# Revit family: KS Husky, Typ IV-19, M 8-M10, Ø 10- 76,1
name_source: partatom
category: HLS-Bauteile
revit_build: Autodesk Revit 2017 (Build: 20190507_1515(x64)
units: mm (PartAtom-declared; Revit-internal decimal feet)

## family parameters
Arbeitsebenenbasiert = Ja
Beim Laden mit Abzugskörper schneiden = Nein
Bemaßung runder Anschluss = Durchmesser verwenden
Gemeinsam genutzt = Ja
Immer vertikal = Nein
Raumberechnungspunkt = Nein
Teiletyp = Normal

## types (20) — shared parameters
Anschluss = M8/M10
Baustoffklasse = B2
DVS = 5 mm  [stored 0.0164042 ft]
Dichte Kern = 120 kg/m³
Dämmkörper = KA/PU
Fabrikat = MEFA
Firma = MEFA Befestigungs- und Montagesysteme GmbH
H1 = 2 mm  [stored 0.00656168 ft]
HGA = 16 mm  [stored 0.0524934 ft]
Kurztext1 = Kälteschelle Husky IV 19
Material = Stahl
Material Mantel = Kunststoff
Materialname = DD11
Mengeneinheit = St
Oberflaeche = galvanisch verzinkt
Rohrschellentyp = Trabant
Typ = IV 19
Vorgabe-Ansicht = 1219 mm
Wasserdampfdiffusionswiderstand = 7000 µ
Wärmeleitfähigkeit = 0.029 W/mK
max. Temperaturbeständigkeit = 105 °C
mittl. Nenndruckfestigkeit Kern = 1,35 N/mm²
stat. Belastung Kern = 0,27 N/mm²

## per-type parameters (varying)
- Kälteschelle Husky, Typ IV-19, M8/M10, Ø 10: A=38 mm  [stored 0.124672 ft]; Anschlußhöhe=39 mm; Artikelnummer=6840100; B=92 mm; Breite=88 mm; D=10 mm  [stored 0.0328084 ft]; D0=51 mm  [stored 0.167323 ft]; DF1=19 mm  [stored 0.062336 ft]; DF2=19 mm  [stored 0.062336 ft]; DS=21 mm  [stored 0.0688976 ft]; Dämmstärke=21 mm  [stored 0.0688976 ft]; EAN=4250928454652; Gewicht=0.09 kg; Gewicht pro Bauteil=0.09 kg; H=70 mm; H2=3 mm  [stored 0.00984252 ft]; Kurztext2=10 mm Iso 21 x 36 mm M8/M10; L=36 mm  [stored 0.11811 ft]; MB=20 mm  [stored 0.0656168 ft]; MD=2 mm  [stored 0.00656168 ft]; R=26 mm; RM=27 mm  [stored 0.0885827 ft]; Rohraußendurchmesser Kunststoff=10 mm; Rohraußendurchmesser Kupfer=10 mm; S=73 mm; Schalenlänge=36 mm; max. zul. Last=0.10 kN; vpe=24 St
- Kälteschelle Husky, Typ IV-19, M8/M10, Ø 12: A=37 mm  [stored 0.121391 ft]; Anschlußhöhe=38 mm; Artikelnummer=6840120; B=92 mm; Breite=88 mm; D=12 mm  [stored 0.0393701 ft]; D0=51 mm  [stored 0.167323 ft]; DF1=19 mm  [stored 0.062336 ft]; DF2=19 mm  [stored 0.062336 ft]; DS=20 mm  [stored 0.0656168 ft]; Dämmstärke=20 mm  [stored 0.0656168 ft]; EAN=4250928440662; Gewicht=0.09 kg; Gewicht pro Bauteil=0.09 kg; H=70 mm; H2=3 mm  [stored 0.00984252 ft]; Kurztext2=12 mm Iso 20 x 36 mm M8/M10; L=36 mm  [stored 0.11811 ft]; MB=20 mm  [stored 0.0656168 ft]; MD=2 mm  [stored 0.00656168 ft]; R=26 mm; RM=27 mm  [stored 0.0885827 ft]; Rohraußendurchmesser Kunststoff=12 mm; Rohraußendurchmesser Kupfer=12 mm; S=73 mm; Schalenlänge=36 mm; max. zul. Last=0.10 kN; vpe=24 St
- Kälteschelle Husky, Typ IV-19, M8/M10, Ø 15: A=36 mm  [stored 0.11811 ft]; Anschlußhöhe=37 mm; Artikelnummer=6840150; B=92 mm; Breite=88 mm; D=15 mm  [stored 0.0492126 ft]; D0=51 mm  [stored 0.167323 ft]; DF1=19 mm  [stored 0.062336 ft]; DF2=19 mm  [stored 0.062336 ft]; DS=18 mm  [stored 0.0590551 ft]; Dämmstärke=18 mm  [stored 0.0590551 ft]; EAN=4250928440679; Gewicht=0.09 kg; Gewicht pro Bauteil=0.09 kg; H=70 mm; H2=3 mm  [stored 0.00984252 ft]; Kurztext2=15 mm Iso 18 x 36 mm M8/M10; L=36 mm  [stored 0.11811 ft]; MB=20 mm  [stored 0.0656168 ft]; MD=2 mm  [stored 0.00656168 ft]; R=26 mm; RM=27 mm  [stored 0.0885827 ft]; Rohraußendurchmesser Kunststoff=15 mm; Rohraußendurchmesser Kupfer=15 mm; S=73 mm; Schalenlänge=36 mm; max. zul. Last=0.13 kN; vpe=24 St
- Kälteschelle Husky, Typ IV-19, M8/M10, Ø 17,2: A=35 mm  [stored 0.114829 ft]; Anschlußhöhe=38 mm; Artikelnummer=6840180; B=92 mm; Breite=94 mm; D=18 mm  [stored 0.0590551 ft]; D0=52 mm; DF1=19 mm  [stored 0.062336 ft]; DF2=18 mm  [stored 0.0590551 ft]; DS=17 mm  [stored 0.0557743 ft]; Dämmstärke=19 mm  [stored 0.062336 ft]; EAN=4250928440686; Gewicht=0.10 kg; Gewicht pro Bauteil=0.10 kg; H=71 mm; H2=3 mm  [stored 0.00984252 ft]; Kurztext2=17,2 mm Iso 19 x 36 mm M8/M10; L=36 mm  [stored 0.11811 ft]; MB=20 mm  [stored 0.0656168 ft]; MD=2 mm  [stored 0.00656168 ft]; R=26 mm; RM=28 mm  [stored 0.0918635 ft]; Rohraußendurchmesser Kunststoff=18 mm; Rohraußendurchmesser Kupfer=18 mm; Rohraußendurchmesser Stahl=17,2 mm; S=73 mm; Schalenlänge=36 mm; max. zul. Last=0.15 kN; vpe=12 St
- Kälteschelle Husky, Typ IV-19, M8/M10, Ø 21,3: A=36 mm  [stored 0.11811 ft]; Anschlußhöhe=39 mm; Artikelnummer=6840220; B=98 mm; Breite=102 mm; D=22 mm  [stored 0.0721785 ft]; D0=58 mm; DF1=19 mm  [stored 0.062336 ft]; DF2=18 mm  [stored 0.0590551 ft]; DS=18 mm  [stored 0.0590551 ft]; Dämmstärke=20 mm  [stored 0.0656168 ft]; EAN=4250928440693; Gewicht=0.11 kg; Gewicht pro Bauteil=0.11 kg; H=77 mm; H2=3 mm  [stored 0.00984252 ft]; Kurztext2=21,3 mm Iso 20 x 36 mm M8/M10; L=36 mm  [stored 0.11811 ft]; MB=20 mm  [stored 0.0656168 ft]; MD=2 mm  [stored 0.00656168 ft]; R=29 mm; RM=31 mm; Rohraußendurchmesser Kupfer=22 mm; Rohraußendurchmesser Stahl=21,3 mm; S=79 mm; Schalenlänge=36 mm; max. zul. Last=0.19 kN; vpe=12 St
- Kälteschelle Husky, Typ IV-19, M8/M10, Ø 26,9: A=36 mm  [stored 0.11811 ft]; Anschlußhöhe=39 mm; Artikelnummer=6840270; B=104 mm; Breite=109 mm; D=27 mm  [stored 0.0885827 ft]; D0=63 mm; DF1=19 mm  [stored 0.062336 ft]; DF2=19 mm  [stored 0.062336 ft]; DS=18 mm  [stored 0.0590551 ft]; Dämmstärke=21 mm  [stored 0.0688976 ft]; EAN=4250928440709; Gewicht=0.11 kg; Gewicht pro Bauteil=0.11 kg; H=82 mm; H2=3 mm  [stored 0.00984252 ft]; Kurztext2=26,9 mm Iso 21 x 36 mm M8/M10; L=36 mm  [stored 0.11811 ft]; MB=20 mm  [stored 0.0656168 ft]; MD=2 mm  [stored 0.00656168 ft]; R=31 mm; RM=33 mm; Rohraußendurchmesser Stahl=26,9 mm; S=85 mm; Schalenlänge=36 mm; max. zul. Last=0.23 kN; vpe=12 St
- Kälteschelle Husky, Typ IV-19, M8/M10, Ø 28: A=38 mm  [stored 0.124672 ft]; Anschlußhöhe=39 mm; Artikelnummer=6840280; B=104 mm; Breite=109 mm; D=28 mm  [stored 0.0918635 ft]; D0=68 mm; DF1=16 mm  [stored 0.0524934 ft]; DF2=17 mm  [stored 0.0557743 ft]; DS=20 mm  [stored 0.0656168 ft]; Dämmstärke=20 mm  [stored 0.0656168 ft]; EAN=4250928440716; Gewicht=0.11 kg; Gewicht pro Bauteil=0.11 kg; H=87 mm; H2=3 mm  [stored 0.00984252 ft]; Kurztext2=28 mm Iso 20 x 36 mm M8/M10; L=36 mm  [stored 0.11811 ft]; MB=20 mm  [stored 0.0656168 ft]; MD=2 mm  [stored 0.00656168 ft]; R=34 mm; RM=36 mm  [stored 0.11811 ft]; Rohraußendurchmesser Kupfer=28 mm; S=88 mm; Schalenlänge=36 mm; max. zul. Last=0.24 kN; vpe=12 St
- Kälteschelle Husky, Typ IV-19, M8/M10, Ø 31,8: A=37 mm  [stored 0.121391 ft]; Anschlußhöhe=38 mm; Artikelnummer=6840320; B=111 mm; Breite=109 mm; D=32 mm  [stored 0.104987 ft]; D0=71 mm; DF1=19 mm  [stored 0.062336 ft]; DF2=18 mm  [stored 0.0590551 ft]; DS=20 mm  [stored 0.0656168 ft]; Dämmstärke=20 mm  [stored 0.0656168 ft]; EAN=4250928440723; Gewicht=0.12 kg; Gewicht pro Bauteil=0.12 kg; H=90 mm; H2=3 mm  [stored 0.00984252 ft]; Kurztext2=31,8 mm Iso 20 x 36 mm M8/M10; L=36 mm  [stored 0.11811 ft]; MB=20 mm  [stored 0.0656168 ft]; MD=2 mm  [stored 0.00656168 ft]; R=36 mm  [stored 0.11811 ft]; RM=37 mm  [stored 0.121391 ft]; Rohraußendurchmesser Kunststoff=32 mm; Rohraußendurchmesser Stahl=31,8 mm; S=92 mm; Schalenlänge=36 mm; max. zul. Last=0.27 kN; vpe=12 St
- Kälteschelle Husky, Typ IV-19, M8/M10, Ø 33,7: A=37 mm  [stored 0.121391 ft]; Anschlußhöhe=38 mm; Artikelnummer=6840340; B=111 mm; Breite=109 mm; D=34 mm; D0=73 mm; DF1=18 mm  [stored 0.0590551 ft]; DF2=17 mm  [stored 0.0557743 ft]; DS=20 mm  [stored 0.0656168 ft]; Dämmstärke=20 mm  [stored 0.0656168 ft]; EAN=4250928440730; Gewicht=0.12 kg; Gewicht pro Bauteil=0.12 kg; H=92 mm; H2=3 mm  [stored 0.00984252 ft]; Kurztext2=33,7 mm Iso 20 x 36 mm M8/M10; L=36 mm  [stored 0.11811 ft]; MB=20 mm  [stored 0.0656168 ft]; MD=2 mm  [stored 0.00656168 ft]; R=37 mm  [stored 0.121391 ft]; RM=38 mm  [stored 0.124672 ft]; Rohraußendurchmesser Stahl=33,7 mm; S=93 mm; Schalenlänge=36 mm; max. zul. Last=0.29 kN; vpe=12 St
- Kälteschelle Husky, Typ IV-19, M8/M10, Ø 35: A=39 mm; Anschlußhöhe=40 mm; Artikelnummer=6840350; B=122 mm; Breite=121 mm; D=35 mm  [stored 0.114829 ft]; D0=77 mm; DF1=21 mm  [stored 0.0688976 ft]; DF2=21 mm  [stored 0.0688976 ft]; DS=21 mm  [stored 0.0688976 ft]; Dämmstärke=21 mm  [stored 0.0688976 ft]; EAN=4250928440747; Gewicht=0.15 kg; Gewicht pro Bauteil=0.15 kg; H=96 mm; H2=3 mm  [stored 0.00984252 ft]; Kurztext2=35 mm Iso 21 x 42 mm M8/M10; L=42 mm  [stored 0.137795 ft]; MB=25 mm  [stored 0.082021 ft]; MD=2 mm  [stored 0.00656168 ft]; R=39 mm; RM=40 mm  [stored 0.131234 ft]; Rohraußendurchmesser Kupfer=35 mm; S=101 mm; Schalenlänge=42 mm; max. zul. Last=0.35 kN; vpe=12 St
- Kälteschelle Husky, Typ IV-19, M8/M10, Ø 40: A=39 mm; Anschlußhöhe=40 mm; Artikelnummer=6840400; B=127 mm; Breite=124 mm; D=40 mm  [stored 0.131234 ft]; D0=82 mm; DF1=21 mm  [stored 0.0688976 ft]; DF2=21 mm  [stored 0.0688976 ft]; DS=21 mm  [stored 0.0688976 ft]; Dämmstärke=21 mm  [stored 0.0688976 ft]; EAN=4250928440754; Gewicht=0.15 kg; Gewicht pro Bauteil=0.15 kg; H=101 mm; H2=3 mm  [stored 0.00984252 ft]; Kurztext2=40 mm Iso 21 x 42 mm M8/M10; L=42 mm  [stored 0.137795 ft]; MB=25 mm  [stored 0.082021 ft]; MD=2 mm  [stored 0.00656168 ft]; R=41 mm  [stored 0.134514 ft]; RM=43 mm; Rohraußendurchmesser Kunststoff=40 mm; S=106 mm; Schalenlänge=42 mm; max. zul. Last=0.40 kN; vpe=12 St
- Kälteschelle Husky, Typ IV-19, M8/M10, Ø 42,4: A=39 mm; Anschlußhöhe=40 mm; Artikelnummer=6840420; B=127 mm; Breite=124 mm; D=42 mm  [stored 0.137795 ft]; D0=86 mm; DF1=19 mm  [stored 0.062336 ft]; DF2=20 mm  [stored 0.0656168 ft]; DS=22 mm  [stored 0.0721785 ft]; Dämmstärke=22 mm  [stored 0.0721785 ft]; EAN=4250928440761; Gewicht=0.16 kg; Gewicht pro Bauteil=0.16 kg; H=105 mm; H2=3 mm  [stored 0.00984252 ft]; Kurztext2=42,4 mm Iso 22 x 42 mm M8/M10; L=42 mm  [stored 0.137795 ft]; MB=25 mm  [stored 0.082021 ft]; MD=2 mm  [stored 0.00656168 ft]; R=43 mm; RM=44 mm; Rohraußendurchmesser Kupfer=42 mm; Rohraußendurchmesser Stahl=42,4 mm; S=108 mm; Schalenlänge=42 mm; max. zul. Last=0.42 kN; vpe=12 St
- Kälteschelle Husky, Typ IV-19, M8/M10, Ø 48,3: A=41 mm  [stored 0.134514 ft]; Anschlußhöhe=42 mm; Artikelnummer=6840480; B=134 mm; Breite=134 mm; D=48 mm  [stored 0.15748 ft]; D0=95 mm; DF1=18 mm  [stored 0.0590551 ft]; DF2=17 mm  [stored 0.0557743 ft]; DS=23 mm  [stored 0.0754593 ft]; Dämmstärke=23 mm  [stored 0.0754593 ft]; EAN=4250928440778; Gewicht=0.21 kg; Gewicht pro Bauteil=0.21 kg; H=115 mm; H2=4 mm  [stored 0.0131234 ft]; Kurztext2=48,3 mm Iso 23 x 42 mm M8/M10; L=42 mm  [stored 0.137795 ft]; MB=25 mm  [stored 0.082021 ft]; MD=2 mm  [stored 0.00656168 ft]; R=48 mm  [stored 0.15748 ft]; RM=50 mm  [stored 0.164042 ft]; Rohraußendurchmesser Stahl=48,3 mm; S=116 mm; Schalenlänge=42 mm; max. zul. Last=0.48 kN; vpe=10 St
- Kälteschelle Husky, Typ IV-19, M8/M10, Ø 50: A=41 mm  [stored 0.134514 ft]; Anschlußhöhe=41 mm; Artikelnummer=6840500; B=134 mm; Breite=134 mm; D=50 mm  [stored 0.164042 ft]; D0=95 mm; DF1=18 mm  [stored 0.0590551 ft]; DF2=17 mm  [stored 0.0557743 ft]; DS=23 mm  [stored 0.0754593 ft]; Dämmstärke=23 mm  [stored 0.0754593 ft]; EAN=4250928440785; Gewicht=0.21 kg; Gewicht pro Bauteil=0.21 kg; H=115 mm; H2=4 mm  [stored 0.0131234 ft]; Kurztext2=50 mm Iso 23 x 42 mm M8/M10; L=42 mm  [stored 0.137795 ft]; MB=25 mm  [stored 0.082021 ft]; MD=2 mm  [stored 0.00656168 ft]; R=48 mm  [stored 0.15748 ft]; RM=50 mm  [stored 0.164042 ft]; Rohraußendurchmesser Kunststoff=50 mm; S=116 mm; Schalenlänge=42 mm; max. zul. Last=0.49 kN; vpe=10 St
- Kälteschelle Husky, Typ IV-19, M8/M10, Ø 54: A=40 mm  [stored 0.131234 ft]; Anschlußhöhe=40 mm; Artikelnummer=6840540; B=134 mm; Breite=134 mm; D=54 mm; D0=97 mm; DF1=17 mm  [stored 0.0557743 ft]; DF2=16 mm  [stored 0.0524934 ft]; DS=22 mm  [stored 0.0721785 ft]; Dämmstärke=22 mm  [stored 0.0721785 ft]; EAN=4250928440792; Gewicht=0.21 kg; Gewicht pro Bauteil=0.21 kg; H=117 mm; H2=4 mm  [stored 0.0131234 ft]; Kurztext2=54 mm Iso 22 x 42 mm M8/M10; L=42 mm  [stored 0.137795 ft]; MB=25 mm  [stored 0.082021 ft]; MD=2 mm  [stored 0.00656168 ft]; R=49 mm; RM=51 mm  [stored 0.167323 ft]; Rohraußendurchmesser Kupfer=54 mm; S=117 mm; Schalenlänge=42 mm; max. zul. Last=0.53 kN; vpe=10 St
- Kälteschelle Husky, Typ IV-19, M8/M10, Ø 57: A=44 mm; Anschlußhöhe=42 mm; Artikelnummer=6840571; B=153 mm; Breite=153 mm; D=57 mm; D0=108 mm; DF1=20 mm  [stored 0.0656168 ft]; DF2=20 mm  [stored 0.0656168 ft]; DS=26 mm; Dämmstärke=26 mm; EAN=4250928440808; Gewicht=0.28 kg; Gewicht pro Bauteil=0.28 kg; H=129 mm; H2=4 mm  [stored 0.0131234 ft]; Kurztext2=57 mm Iso 26 x 42 mm M8/M10; L=42 mm  [stored 0.137795 ft]; MB=25 mm  [stored 0.082021 ft]; MD=3 mm  [stored 0.00984252 ft]; R=54 mm; RM=57 mm; Rohraußendurchmesser Stahl=57 mm; S=133 mm; Schalenlänge=42 mm; max. zul. Last=0.56 kN; vpe=8 St
- Kälteschelle Husky, Typ IV-19, M8/M10, Ø 60,3: A=42 mm  [stored 0.137795 ft]; Anschlußhöhe=42 mm; Artikelnummer=6840601; B=153 mm; Breite=153 mm; D=60 mm; D0=108 mm; DF1=20 mm  [stored 0.0656168 ft]; DF2=20 mm  [stored 0.0656168 ft]; DS=24 mm  [stored 0.0787402 ft]; Dämmstärke=24 mm  [stored 0.0787402 ft]; EAN=4250928440815; Gewicht=0.28 kg; Gewicht pro Bauteil=0.28 kg; H=129 mm; H2=4 mm  [stored 0.0131234 ft]; Kurztext2=60,3 mm Iso 24 x 42 mm M8/M10; L=42 mm  [stored 0.137795 ft]; MB=25 mm  [stored 0.082021 ft]; MD=3 mm  [stored 0.00984252 ft]; R=54 mm; RM=57 mm; Rohraußendurchmesser Stahl=60,3 mm; S=133 mm; Schalenlänge=42 mm; max. zul. Last=0.60 kN; vpe=8 St
- Kälteschelle Husky, Typ IV-19, M8/M10, Ø 63,5: A=42 mm  [stored 0.137795 ft]; Anschlußhöhe=44 mm; Artikelnummer=6840641; B=153 mm; Breite=153 mm; D=64 mm; D0=110 mm; DF1=19 mm  [stored 0.062336 ft]; DF2=19 mm  [stored 0.062336 ft]; DS=23 mm  [stored 0.0754593 ft]; Dämmstärke=23 mm  [stored 0.0754593 ft]; EAN=4250928440822; Gewicht=0.28 kg; Gewicht pro Bauteil=0.28 kg; H=131 mm; H2=4 mm  [stored 0.0131234 ft]; Kurztext2=63,5 mm Iso 23 x 42 mm M8/M10; L=42 mm  [stored 0.137795 ft]; MB=25 mm  [stored 0.082021 ft]; MD=3 mm  [stored 0.00984252 ft]; R=55 mm; RM=58 mm; Rohraußendurchmesser Kupfer=64 mm; Rohraußendurchmesser Stahl=63,5 mm; S=134 mm; Schalenlänge=42 mm; max. zul. Last=0.63 kN; vpe=8 St
- Kälteschelle Husky, Typ IV-19, M8/M10, Ø 70: A=42 mm  [stored 0.137795 ft]; Anschlußhöhe=43 mm; Artikelnummer=6840701; B=166 mm; Breite=165 mm; D=70 mm; D0=117 mm; DF1=22 mm  [stored 0.0721785 ft]; DF2=22 mm  [stored 0.0721785 ft]; DS=24 mm  [stored 0.0787402 ft]; Dämmstärke=24 mm  [stored 0.0787402 ft]; EAN=4250928440839; Gewicht=0.29 kg; Gewicht pro Bauteil=0.29 kg; H=138 mm; H2=4 mm  [stored 0.0131234 ft]; Kurztext2=70 mm Iso 24 x 42 mm M8/M10; L=42 mm  [stored 0.137795 ft]; MB=25 mm  [stored 0.082021 ft]; MD=3 mm  [stored 0.00984252 ft]; R=59 mm; RM=61 mm; Rohraußendurchmesser Stahl=70 mm; S=144 mm; Schalenlänge=42 mm; max. zul. Last=0.69 kN; vpe=8 St
- Kälteschelle Husky, Typ IV-19, M8/M10, Ø 76,1: A=42 mm  [stored 0.137795 ft]; Anschlußhöhe=42 mm; Artikelnummer=6840761; B=166 mm; Breite=165 mm; D=76 mm; D0=123 mm; DF1=19 mm  [stored 0.062336 ft]; DF2=19 mm  [stored 0.062336 ft]; DS=24 mm  [stored 0.0787402 ft]; Dämmstärke=24 mm  [stored 0.0787402 ft]; EAN=4250928440846; Gewicht=0.29 kg; Gewicht pro Bauteil=0.29 kg; H=144 mm; H2=4 mm  [stored 0.0131234 ft]; Kurztext2=76,1 mm Iso 24 x 42 mm M8/M10; L=42 mm  [stored 0.137795 ft]; MB=25 mm  [stored 0.082021 ft]; MD=3 mm  [stored 0.00984252 ft]; R=62 mm; RM=64 mm; Rohraußendurchmesser Stahl=76,1 mm; S=147 mm; Schalenlänge=42 mm; max. zul. Last=0.75 kN; vpe=8 St

note: [stored X ft] marks values corroborated as IEEE doubles in the binary element streams (Revit-internal decimal feet)

## geometry (parser evidence)
native form markers: Sweep x3
no freeform markers — native parametric forms only
